# Revit family: Halter 45-120
name_source: partatom
category: HLS-Bauteile
revit_build: Autodesk Revit 2018 (Build: 20190510_1515(x64)
units: mm (PartAtom-declared; Revit-internal decimal feet)

## family parameters
Basisbauteil = Fläche
Beim Laden mit Abzugskörper schneiden = Nein
Bemaßung runder Anschluss = Durchmesser verwenden
Gemeinsam genutzt = Ja
Raumberechnungspunkt = Nein
Teiletyp = Normal

## types (1)
- Halter 45-120
    Artikelnummer = 08121002
    Ausrichtung Platte = längs
    Befestigung = Baukörper
    Breite Platte = 70 mm  [stored 0.229659 ft]
    EAN = 4250928448606
    Fabrikat = MEFA
    Firma = MEFA Befestigungs- und Montagesysteme GmbH
    Gewicht = 1.54 kg
    Gewicht pro Bauteil = 1.54 kg
    Kurztext1 = Halter Doppel-C-Profil 45 längs
    Kurztext2 = für Doppel-C-Profil 45/120 fsv
    Langloch = 14x20 mm
    Lochabstand = 174 mm
    Länge = 0 mm  [stored 0 ft]
    Länge Platte = 216 mm  [stored 0.708661 ft]
    Material = Stahl
    Mengeneinheit = St
    Oberflaeche = feuerstückverzinkt
    Profil = Doppel-C-Profil
    Profilname = 45/120
    Profiltyp = 45/120
    Sicherheitsfaktor = 0
    Stärke Platte = 8 mm  [stored 0.0262467 ft]
    Vorgabe-Ansicht = 1219 mm
    max. Profilhöhe = 120 mm  [stored 0.393701 ft]
    max. zul. Last Druck = 0.00 kip
    vpe = 5 St

note: [stored X ft] marks values corroborated as IEEE doubles in the binary element streams (Revit-internal decimal feet)
